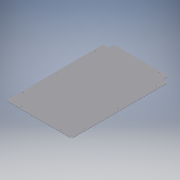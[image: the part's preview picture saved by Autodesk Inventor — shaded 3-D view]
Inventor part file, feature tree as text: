
AUTODESK INVENTOR PART (.ipt)
format: ipt  version: 2016 (Build 200138000, 138)  size: 156,672 bytes
history: native  units: mm
features: sketch x3, hole x2, other x2, plane x1, sheet_metal_op x1
ambient origin geometry x8: Origin, YZ Plane, XZ Plane, XY Plane, X Axis, Y Axis, Z Axis, Center Point
bodies: Body1 (feature_tree)
feature tree (9):
  sketch  "Sketch1"  dims[d26=1.0mm d27=10.0mm]
  plane  "Work Plane1"
  sketch  "Sketch2"  dims[d28=60.0mm d29=60.0mm]
  sheet_metal_op  "Face2"
  hole  "Hole2"  [1 undecoded]
  other  "Corner Chamfer1"
  hole  "Hole3"  [1 undecoded]
  other  "Plate2"
  sketch  "Sketch3"  dims[d30=10.0mm d31=10.0mm d32=60.0mm d33=60.0mm d34=10.0mm d44=25.0mm d45=25.0mm d46=25.0mm d47=25.0mm d48=1.0mm d49=4.0mm d50=6.0mm d51=4.0mm d52=2.0mm d53=90.0deg d54=1.0mm d55=20.594885mm d56=6.0mm d57=6.0mm d58=45.0deg d63=10.0mm d64=60.0mm d65=60.0mm d66=10.0mm d67=70.0mm d68=70.0mm d69=10.0mm d70=10.0mm d71=4.0mm d72=6.0mm d73=4.0mm d74=2.0mm d75=90.0deg d76=1.0mm d77=20.594885mm d80=3.0mm d81=3.0mm d82=3.0mm d83=3.0mm]
note: 2 required parameter values undecoded (feature->parameter linkage not recoverable at this tier; creation-order binding heuristic only, values carry confidence <= 0.55)
